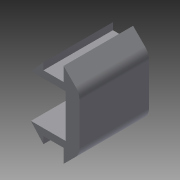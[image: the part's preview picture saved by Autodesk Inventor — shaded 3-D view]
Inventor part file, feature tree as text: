
AUTODESK INVENTOR PART (.ipt)
format: ipt  version: 2015 SP1 (Build 190203100, 203)  size: 99,328 bytes
history: native  units: in
note: dims shown in document units (in); Inventor stores cm internally (conversion verified against a paired STEP export)
features: extrude x1, sketch x1
ambient origin geometry x8: Origin, YZ Plane, XZ Plane, XY Plane, X Axis, Y Axis, Z Axis, Center Point
bodies: Solid1 (feature_tree)
feature tree (2):
  extrude  "Extrusion1"  TaperAngle=45.0deg  [1 undecoded]
  sketch  "Sketch1"  dims[d0=0.0394in d2=45.0deg d3=45.0deg d4=0.0906in d5=0.0906in d6=0.0787in d7=0.0787in d8=0.0394in d9=0.0394in d10=0.1969in d11=0.1969in d12=0.0394in d13=0.0787in d14=0.3937in d15=0.0in d16=0.1142in d17=0.1142in d18=0.0787in]
note: 1 required parameter value undecoded (feature->parameter linkage not recoverable at this tier; creation-order binding heuristic only, values carry confidence <= 0.55)
